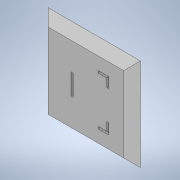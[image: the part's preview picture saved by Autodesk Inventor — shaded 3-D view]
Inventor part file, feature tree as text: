
AUTODESK INVENTOR PART (.ipt)
format: ipt  version: 2021 (Build 250183000, 183)  size: 145,408 bytes
history: native  units: in
note: dims shown in document units (in); Inventor stores cm internally (conversion verified against a paired STEP export)
features: chamfer x3, extrude x2, sketch x2
ambient origin geometry x8: Origin, YZ Plane, XZ Plane, XY Plane, X Axis, Y Axis, Z Axis, Center Point
bodies: Solid1 (feature_tree)
feature tree (7):
  extrude  "Extrusion1"  Depth=0.1575in
  chamfer  "Chamfer1"  Distance=0.1575in
  extrude  "Extrusion2"  Depth=0.1575in
  chamfer  "Chamfer2"  Distance=0.2756in
  chamfer  "Chamfer3"  Distance=1.3386in
  sketch  "Sketch1"  dims[d0=1.7323in d1=1.7323in d2=0.1575in d3=0.0in]
  sketch  "Sketch2"  dims[d4=0.1575in d5=0.0787in d6=45.0deg d7=0.0394in d8=0.2756in d9=1.3386in d10=0.315in d11=0.0394in d12=0.1969in d13=0.3937in d14=0.1969in d15=0.3937in d19=0.1969in d20=0.0394in d21=0.1575in d22=0.1575in d23=0.0394in d24=0.1969in d25=0.1969in d26=0.0197in d27=0.0in d28=0.0197in d29=0.0787in d30=45.0deg d31=0.0197in d32=0.0787in d33=45.0deg]
